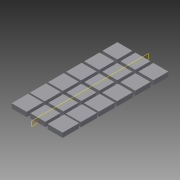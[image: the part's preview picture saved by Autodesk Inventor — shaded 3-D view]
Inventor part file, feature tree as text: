
AUTODESK INVENTOR PART (.ipt)
format: ipt  version: 2013 (Build 170138000, 138)  size: 201,216 bytes
history: native  units: mm
features: projected_geometry x9, extrude x5, sketch x5, pattern_linear x1, plane x1, mirror x1
ambient origin geometry x8: Origin, YZ Plane, XZ Plane, XY Plane, X Axis, Y Axis, Z Axis, Center Point
bodies: Solid1 (feature_tree)
feature tree (22):
  extrude  "Extrusion1"  Depth=10.0mm
  pattern_linear  "Rectangular Pattern1"  Count1=6 Spacing1=12.0mm
  extrude  "Extrusion2"  Depth=10.0mm
  plane  "Work Plane1"
  mirror  "Mirror1"
  extrude  "Extrusion3"  Depth=10.2mm
  extrude  "Extrusion4"  Depth=10.4mm
  extrude  "Extrusion5"  Depth=5.2mm
  sketch  "Sketch1"  dims[d0=10.0mm d2=10.0mm]
  sketch  "Sketch2"  dims[d3=3.0mm d4=0.0mm d5=60.0mm d7=12.0mm]
  projected_geometry  "Projected Loop1"
  projected_geometry  "Projected Loop2"
  projected_geometry  "Projected Loop3"
  projected_geometry  "Projected Loop4"
  projected_geometry  "Projected Loop5"
  sketch  "Sketch3"  dims[d8=12.0mm d10=10.0mm]
  projected_geometry  "Projected Loop6"
  projected_geometry  "Projected Loop7"
  sketch  "Sketch4"  dims[d11=10.0mm d12=10.2mm]
  projected_geometry  "Projected Loop8"
  sketch  "Sketch5"  dims[d13=5.1mm d14=10.4mm d15=5.2mm d16=5.3mm d17=5.4mm d18=10.6mm d19=10.8mm d20=11.0mm d21=5.5mm d22=3.0mm d23=0.0mm d24=3.0mm d25=0.0mm d26=3.0mm d27=0.0mm d28=3.0mm d29=0.0mm]
  projected_geometry  "Projected Loop9"
